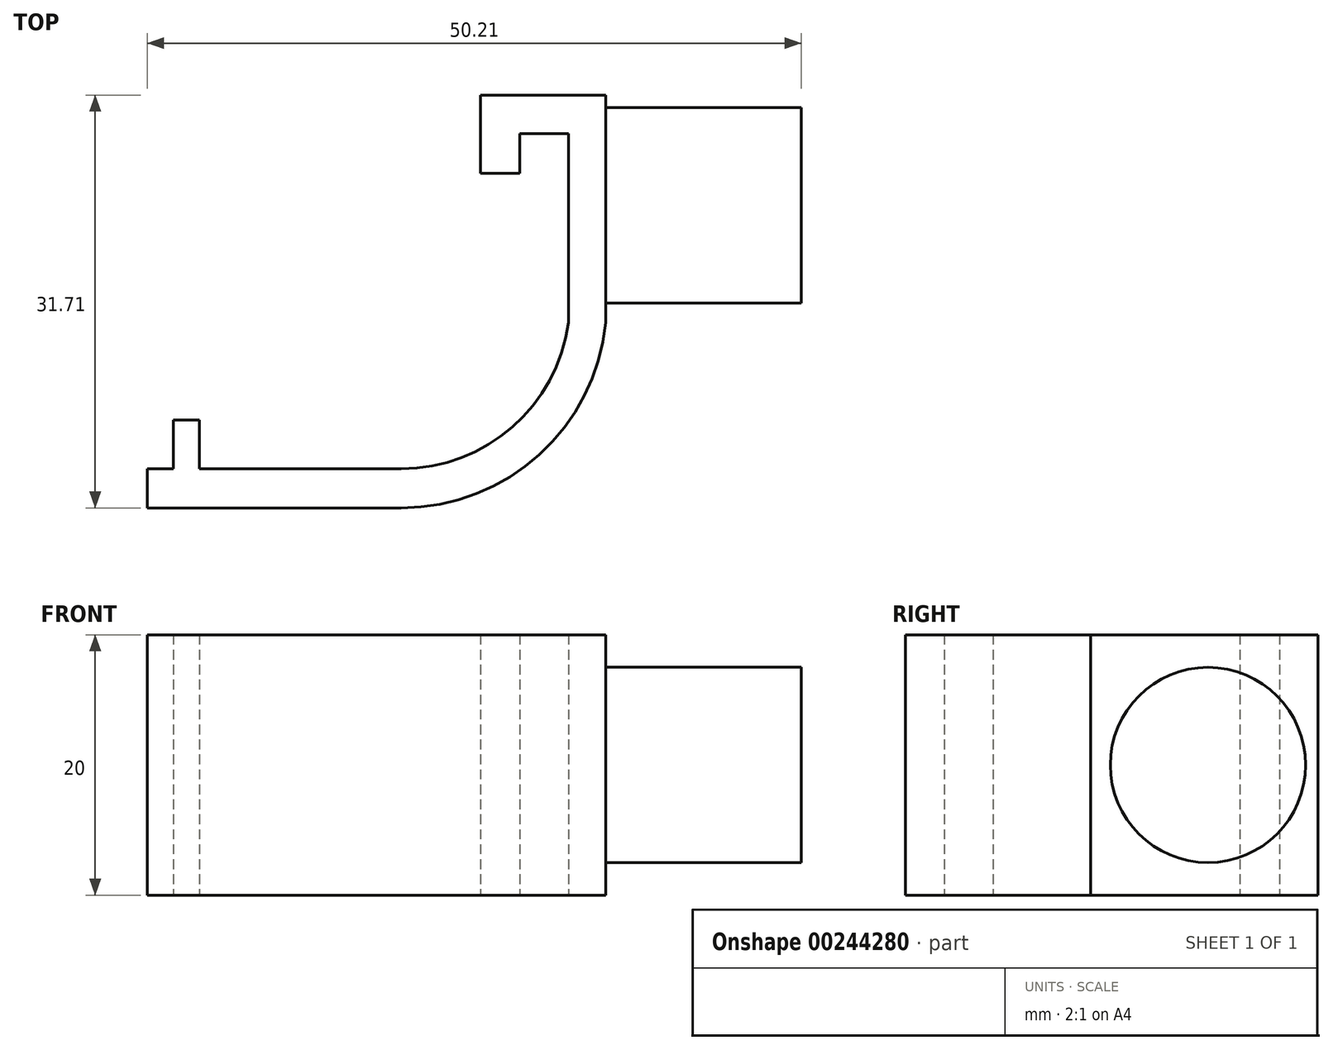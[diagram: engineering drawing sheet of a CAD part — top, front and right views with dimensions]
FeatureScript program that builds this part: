
annotation { "Feature Type Name" : "Feature", "Feature Type Description" : "" }
export const myFeature = defineFeature(function(context is Context, id is Id, definition is map)
    precondition{}
    {
        {
            var Q0;
            Q0=qCreatedBy(makeId("Top.planeOp"),FACE);
            var sketch = newSketch(context, id + "F0", { "sketchPlane" : qUnion([Q0])});
            skLineSegment(sketch, "E0", {"start": v(0, 3.75) * mm, "end": v(2, 3.75) * mm});
            skLineSegment(sketch, "E1", {"start": v(2, 3.75) * mm, "end": v(2, 0) * mm});
            skLineSegment(sketch, "E2", {"start": v(2, 0) * mm, "end": v(17.5, 0) * mm});
            skLineSegment(sketch, "E3", {"start": v(0, 3.75) * mm, "end": v(0, 0) * mm});
            skLineSegment(sketch, "E4", {"start": v(30.34, 25.75) * mm, "end": v(26.59, 25.75) * mm});
            skLineSegment(sketch, "E5", {"start": v(26.59, 25.75) * mm, "end": v(26.59, 22.71) * mm});
            skLineSegment(sketch, "E6", {"start": v(26.59, 22.71) * mm, "end": v(23.59, 22.71) * mm});
            skLineSegment(sketch, "E7", {"start": v(23.59, 22.71) * mm, "end": v(23.59, 28.71) * mm});
            skLineSegment(sketch, "E8", {"start": v(23.59, 28.71) * mm, "end": v(33.21, 28.71) * mm});
            skLineSegment(sketch, "E9", {"start": v(30.34, 25.75) * mm, "end": v(30.34, 11.25) * mm});
            skLineSegment(sketch, "E10", {"start": v(33.21, 28.71) * mm, "end": v(33.21, 11.25) * mm});
            skLineSegment(sketch, "E11", {"start": v(0, -3) * mm, "end": v(17.5, -3) * mm});
            skArc(sketch, "E12", {"start": v(17.5, 0) * mm, "mid": v(26.03, 3.21) * mm, "end": v(30.34, 11.25) * mm});
            skArc(sketch, "E13", {"start": v(17.5, -3) * mm, "mid": v(28.1, 1.1) * mm, "end": v(33.21, 11.25) * mm});
            skLineSegment(sketch, "E14.bottom", {"start": v(0, -3) * mm, "end": v(-2, -3) * mm});
            skLineSegment(sketch, "E14.top", {"start": v(0, 0) * mm, "end": v(-2, 0) * mm});
            skLineSegment(sketch, "E14.right", {"start": v(-2, -3) * mm, "end": v(-2, 0) * mm});
            skSolve(sketch);
        }
        {
            var Q0;
            Q0=makeQuery(id+"F0.imprint","IMPRINT",FACE,{"disambiguationData":[TD([[makeQuery(id+"F0.imprint","IMPRINT",EDGE,{"derivedFrom":sQuery(id+"F0.wireOp",EDGE,"E0")}),-1.0]])]});
            extrude(context, id + "F1", {"entities" : qUnion([Q0]), "depth" : 20 * mm});
        }
        {
            var Q0;
            Q0=makeQuery(id+"F1.opExtrude","SWEPT_FACE",FACE,{"disambiguationData":[OSD([sQuery(id+"F0.wireOp",EDGE,"E10")])]});
            var sketch = newSketch(context, id + "F2", { "sketchPlane" : qUnion([Q0])});
            skCircle(sketch, "E15", {"center": v(20.25, 10) * mm, "radius": 7.5 * mm});
            skPoint(sketch, "E15.centerSnap0", {"position": v(28.71, 10) * mm});
            skSolve(sketch);
        }
        {
            var Q0;
            Q0=makeQuery(id+"F2.imprint","IMPRINT",FACE,{"disambiguationData":[TD([[makeQuery(id+"F2.imprint","IMPRINT",EDGE,{"derivedFrom":sQuery(id+"F2.wireOp",EDGE,"E15")}),1.0]])]});
            extrude(context, id + "F3", {"entities" : qUnion([Q0]), "operationType" : NewBodyOperationType.ADD, "depth" : 15 * mm});
        }
    });
